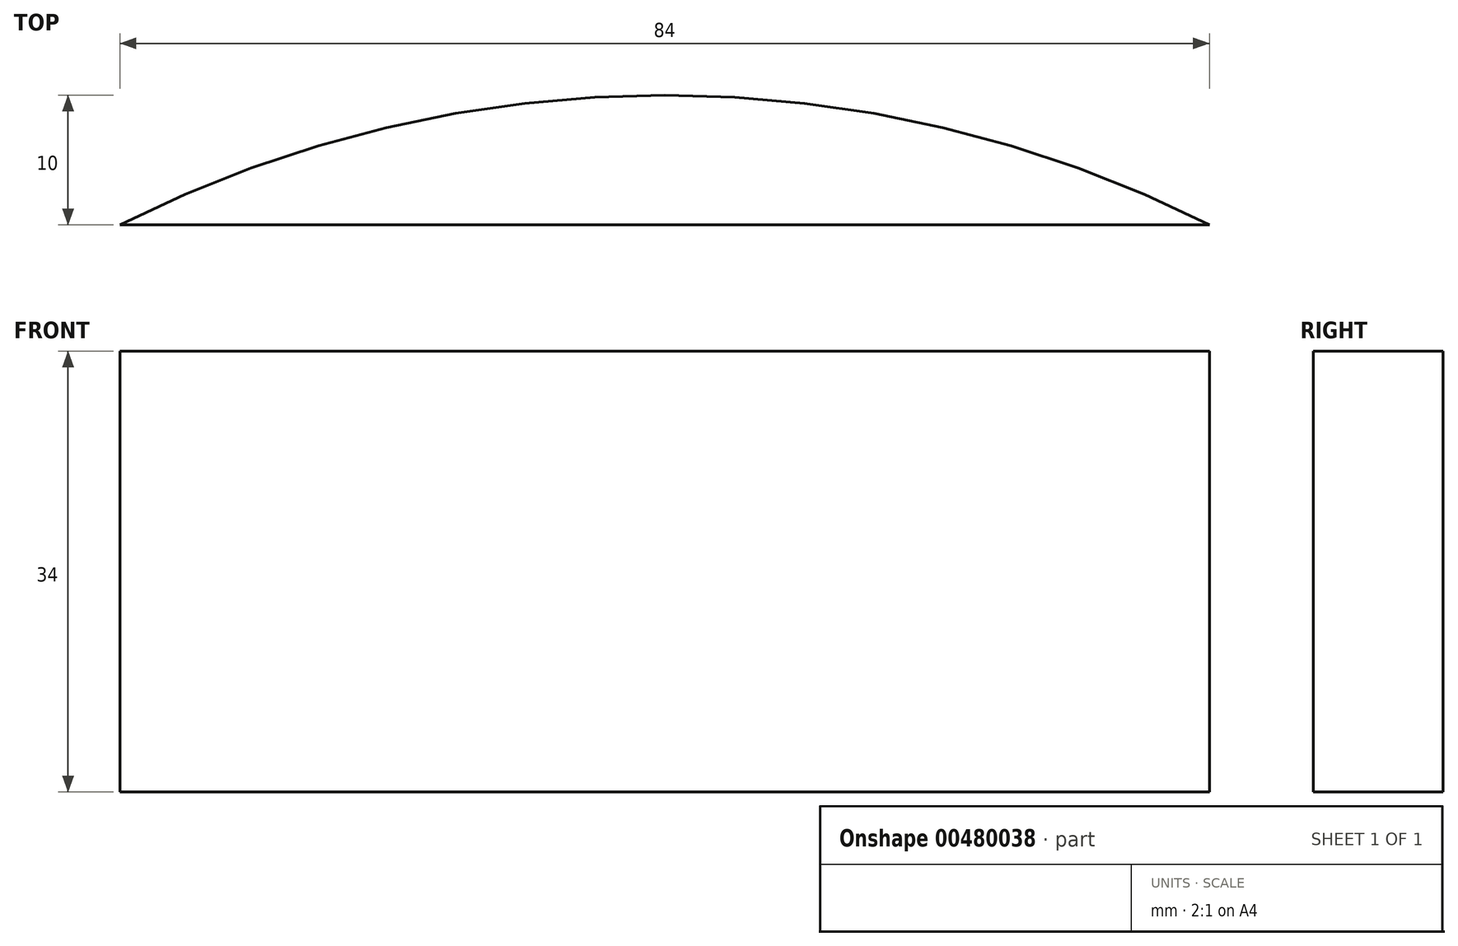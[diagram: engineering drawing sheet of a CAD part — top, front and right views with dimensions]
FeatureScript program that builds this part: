
annotation { "Feature Type Name" : "Feature", "Feature Type Description" : "" }
export const myFeature = defineFeature(function(context is Context, id is Id, definition is map)
    precondition{}
    {
        {
            var Q0;
            Q0=qCreatedBy(makeId("Top.planeOp"),FACE);
            var sketch = newSketch(context, id + "F0", { "sketchPlane" : qUnion([Q0])});
            skLineSegment(sketch, "E0", {"start": v(-52.77, -4.06) * mm, "end": v(31.23, -4.06) * mm});
            skLineSegment(sketch, "E1", {"start": v(-10.77, -4.06) * mm, "end": v(-10.77, 5.94) * mm, "construction": true});
            skArc(sketch, "E2", {"start": v(31.23, -4.06) * mm, "mid": v(-10.77, 5.94) * mm, "end": v(-52.77, -4.06) * mm});
            skSolve(sketch);
        }
        {
            var Q0;
            Q0=qSketchRegion(id+"F0",true);
            extrude(context, id + "F1", {"entities" : qUnion([Q0]), "depth" : 34 * mm});
        }
    });
